# Revit family: Gewindestift VA
name_source: partatom
category: HLS-Bauteile
revit_build: Autodesk Revit 2017 (Build: 20190507_1515(x64)
units: mm (PartAtom-declared; Revit-internal decimal feet)

## family parameters
Arbeitsebenenbasiert = Nein
Beim Laden mit Abzugskörper schneiden = Nein
Bemaßung runder Anschluss = Durchmesser verwenden
Gemeinsam genutzt = Ja
Immer vertikal = Nein
Raumberechnungspunkt = Nein
Teiletyp = Normal

## types (11) — shared parameters
Fabrikat = MEFA
Firma = MEFA Befestigungs- und Montagesysteme GmbH
Material = Edelstahl
Mengeneinheit = St

## per-type parameters (varying)
| type | Artikelnummer | D | EAN | Gewicht | Gewicht pro Bauteil | Kurztext1 | Kurztext2 | L | vpe |
| Gewindestift M 8x 30 V2A | 0732130 | 7 mm  [stored 0.0229659 ft] | 4250928416834 | 0.01 kg | 0.01 kg | Gewindestift DIN 976-1 V2A | M8 x 30 mm | 30 mm  [stored 0.0984252 ft] | 100 St |
| Gewindestift M 8x 50 V2A | 0732150 | 7 mm  [stored 0.0229659 ft] | 4250928416841 | 0.02 kg | 0.02 kg | Gewindestift DIN 976-1 V2A | M8 x 50 mm | 50 mm  [stored 0.164042 ft] | 100 St |
| Gewindestift M 8x 70 V2A | 0732170 | 7 mm  [stored 0.0229659 ft] | 4250928416858 | 0.02 kg | 0.02 kg | Gewindestift DIN 976-1 V2A | M8 x 70 mm | 70 mm  [stored 0.229659 ft] | 100 St |
| Gewindestift M 8x110 V2A | 0732210 | 7 mm  [stored 0.0229659 ft] | 4250928416865 | 0.04 kg | 0.04 kg | Gewindestift DIN 976-1 V2A | M8 x 110 mm | 110 mm  [stored 0.360892 ft] | 100 St |
| Gewindestift M10x 50 V2A | 0732350 | 8 mm  [stored 0.0262467 ft] | 4250928416872 | 0.03 kg | 0.03 kg | Gewindestift DIN 976-1 V2A | M10 x 50 mm | 50 mm  [stored 0.164042 ft] | 100 St |
| Gewindestift M10x 70 V2A | 0732370 | 8 mm  [stored 0.0262467 ft] | 4250928416889 | 0.04 kg | 0.04 kg | Gewindestift DIN 976-1 V2A | M10 x 70 mm | 70 mm  [stored 0.229659 ft] | 100 St |
| Gewindestift M10x110 V2A | 0732410 | 8 mm  [stored 0.0262467 ft] | 4250928416896 | 0.06 kg | 0.06 kg | Gewindestift DIN 976-1 V2A | M10 x 110 mm | 110 mm  [stored 0.360892 ft] | 50 St |
| Gewindestift M12x 50 V2A | 0732550 | 10 mm  [stored 0.0328084 ft] | 4250928416902 | 0.04 kg | 0.04 kg | Gewindestift DIN 976-1 V2A | M12 x 50 mm | 50 mm  [stored 0.164042 ft] | 50 St |
| Gewindestift M12x110 V2A | 0732610 | 10 mm  [stored 0.0328084 ft] | 4250928416919 | 0.08 kg | 0.08 kg | Gewindestift DIN 976-1 V2A | M12 x 110 mm | 110 mm  [stored 0.360892 ft] | 50 St |
| Gewindestift M12x 50 V4A | 0734550 | 10 mm  [stored 0.0328084 ft] | 4250928416933 | 0.04 kg | 0.04 kg | Gewindestift DIN 976-1 V4A | M12 x 50 mm | 50 mm  [stored 0.164042 ft] | 50 St |
| Gewindestift M12x110 V4A | 0734610 | 10 mm  [stored 0.0328084 ft] | 4250928416940 | 0.08 kg | 0.08 kg | Gewindestift DIN 976-1 V4A | M12 x 110 mm | 110 mm  [stored 0.360892 ft] | 50 St |

note: [stored X ft] marks values corroborated as IEEE doubles in the binary element streams (Revit-internal decimal feet)
